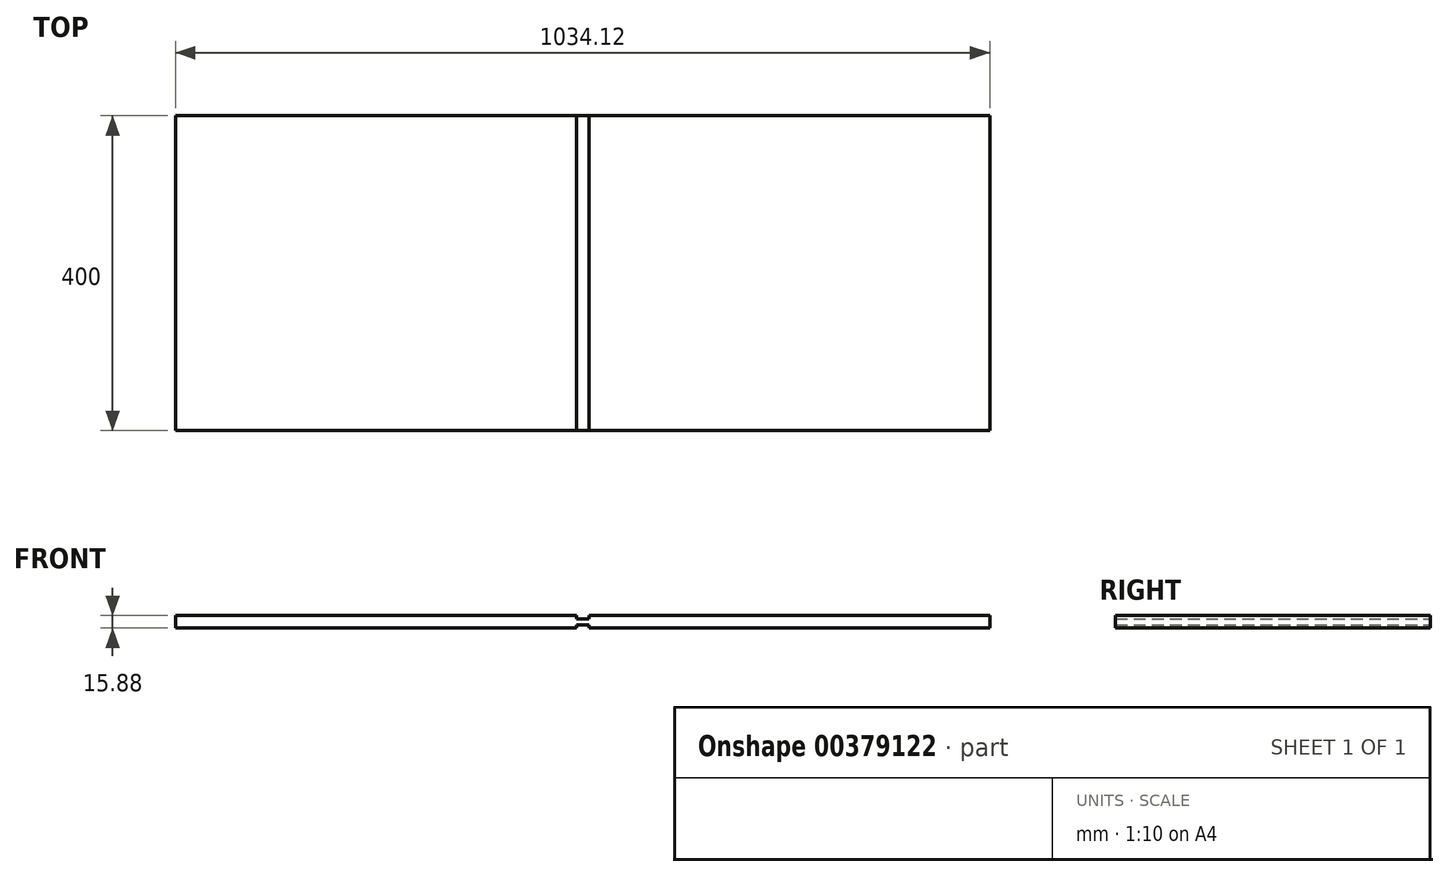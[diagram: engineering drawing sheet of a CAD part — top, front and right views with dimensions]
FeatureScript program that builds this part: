
annotation { "Feature Type Name" : "Feature", "Feature Type Description" : "" }
export const myFeature = defineFeature(function(context is Context, id is Id, definition is map)
    precondition{}
    {
        {
            var Q0;
            Q0=qCreatedBy(makeId("Front.planeOp"),FACE);
            var sketch = newSketch(context, id + "F0", { "sketchPlane" : qUnion([Q0])});
            skLineSegment(sketch, "E0.bottom", {"start": v(525, 7.94) * mm, "end": v(-525, 7.94) * mm});
            skLineSegment(sketch, "E0.top", {"start": v(525, -7.94) * mm, "end": v(-525, -7.94) * mm});
            skLineSegment(sketch, "E0.left", {"start": v(525, 7.94) * mm, "end": v(525, -7.94) * mm});
            skLineSegment(sketch, "E0.right", {"start": v(-525, 7.94) * mm, "end": v(-525, -7.94) * mm});
            skPoint(sketch, "E0.middle", {"position": v(0, 0) * mm});
            skLineSegment(sketch, "E1.bottom", {"start": v(-525, -7.94) * mm, "end": v(-517.06, -7.94) * mm});
            skLineSegment(sketch, "E1.top", {"start": v(-525, 0) * mm, "end": v(-517.06, 0) * mm});
            skLineSegment(sketch, "E1.left", {"start": v(-525, -7.94) * mm, "end": v(-525, 0) * mm});
            skLineSegment(sketch, "E1.right", {"start": v(-517.06, -7.94) * mm, "end": v(-517.06, 0) * mm});
            skLineSegment(sketch, "E2.bottom", {"start": v(525, -7.94) * mm, "end": v(517.06, -7.94) * mm});
            skLineSegment(sketch, "E2.top", {"start": v(525, 0) * mm, "end": v(517.06, 0) * mm});
            skLineSegment(sketch, "E2.left", {"start": v(525, -7.94) * mm, "end": v(525, 0) * mm});
            skLineSegment(sketch, "E2.right", {"start": v(517.06, -7.94) * mm, "end": v(517.06, 0) * mm});
            skLineSegment(sketch, "E3.bottom", {"start": v(7.94, -7.94) * mm, "end": v(-7.94, -7.94) * mm});
            skLineSegment(sketch, "E3.top", {"start": v(7.94, -3.97) * mm, "end": v(-7.94, -3.97) * mm});
            skLineSegment(sketch, "E3.left", {"start": v(7.94, -7.94) * mm, "end": v(7.94, -3.97) * mm});
            skLineSegment(sketch, "E3.right", {"start": v(-7.94, -7.94) * mm, "end": v(-7.94, -3.97) * mm});
            skPoint(sketch, "E3.middle", {"position": v(0, -5.95) * mm});
            skLineSegment(sketch, "E4.MirrorCS", {"start": v(517.06, 7.94) * mm, "end": v(517.06, 0) * mm});
            skLineSegment(sketch, "E5.MirrorCS", {"start": v(525, 7.94) * mm, "end": v(517.06, 7.94) * mm});
            skLineSegment(sketch, "E6.MirrorCS", {"start": v(525, 7.94) * mm, "end": v(525, 0) * mm});
            skLineSegment(sketch, "E7.MirrorCS", {"start": v(-517.06, 7.94) * mm, "end": v(-517.06, 0) * mm});
            skLineSegment(sketch, "E8.MirrorCS", {"start": v(-525, 7.94) * mm, "end": v(-517.06, 7.94) * mm});
            skLineSegment(sketch, "E9.MirrorCS", {"start": v(-525, 7.94) * mm, "end": v(-525, 0) * mm});
            skLineSegment(sketch, "E10.MirrorCS", {"start": v(7.94, 3.97) * mm, "end": v(-7.94, 3.97) * mm});
            skLineSegment(sketch, "E11.MirrorCS", {"start": v(-7.94, 7.94) * mm, "end": v(-7.94, 3.97) * mm});
            skLineSegment(sketch, "E12.MirrorCS", {"start": v(7.94, 7.94) * mm, "end": v(-7.94, 7.94) * mm});
            skLineSegment(sketch, "E13.MirrorCS", {"start": v(7.94, 7.94) * mm, "end": v(7.94, 3.97) * mm});
            skSolve(sketch);
        }
        {
            var Q0;
            Q0=makeQuery(id+"F0.imprint","IMPRINT",FACE,{"disambiguationData":[TD([[makeQuery(id+"F0.imprint","IMPRINT",EDGE,{"derivedFrom":sQuery(id+"F0.wireOp",EDGE,"E0.bottom")}),1.0]])]});
            extrude(context, id + "F1", {"entities" : qUnion([Q0]), "depth" : 406.35 * mm});
        }
        {
            var Q0;
            Q0=qCreatedBy(makeId("Right.planeOp"),FACE);
            var sketch = newSketch(context, id + "F2", { "sketchPlane" : qUnion([Q0])});
            skLineSegment(sketch, "E14.bottom", {"start": v(0, 0) * mm, "end": v(-6.35, 0) * mm});
            skLineSegment(sketch, "E14.top", {"start": v(0, -7.95) * mm, "end": v(-6.35, -7.95) * mm});
            skLineSegment(sketch, "E14.left", {"start": v(0, 0) * mm, "end": v(0, -7.95) * mm});
            skLineSegment(sketch, "E14.right", {"start": v(-6.35, 0) * mm, "end": v(-6.35, -7.95) * mm});
            skLineSegment(sketch, "E15.MirrorCS", {"start": v(-6.35, 0) * mm, "end": v(-6.35, 7.95) * mm});
            skLineSegment(sketch, "E16.MirrorCS", {"start": v(0, 0) * mm, "end": v(0, 7.95) * mm});
            skLineSegment(sketch, "E17.MirrorCS", {"start": v(0, 7.95) * mm, "end": v(-6.35, 7.95) * mm});
            skSolve(sketch);
        }
        {
            var Q0;
            Q0=makeQuery(id+"F2.imprint","IMPRINT",FACE,{"disambiguationData":[TD([[makeQuery(id+"F2.imprint","IMPRINT",EDGE,{"derivedFrom":sQuery(id+"F2.wireOp",EDGE,"E14.bottom")}),1.0]])]});
            var Q1;
            Q1=makeQuery(id+"F2.imprint","IMPRINT",FACE,{"disambiguationData":[TD([[makeQuery(id+"F2.imprint","IMPRINT",EDGE,{"derivedFrom":sQuery(id+"F2.wireOp",EDGE,"E14.bottom")}),-1.0]])]});
            extrude(context, id + "F3", {"entities" : qUnion([Q0, Q1]), "operationType" : NewBodyOperationType.REMOVE, "endBound" : BoundingType.SYMMETRIC, "oppositeDirection" : true, "depth" : 1050 * mm});
        }
    });
